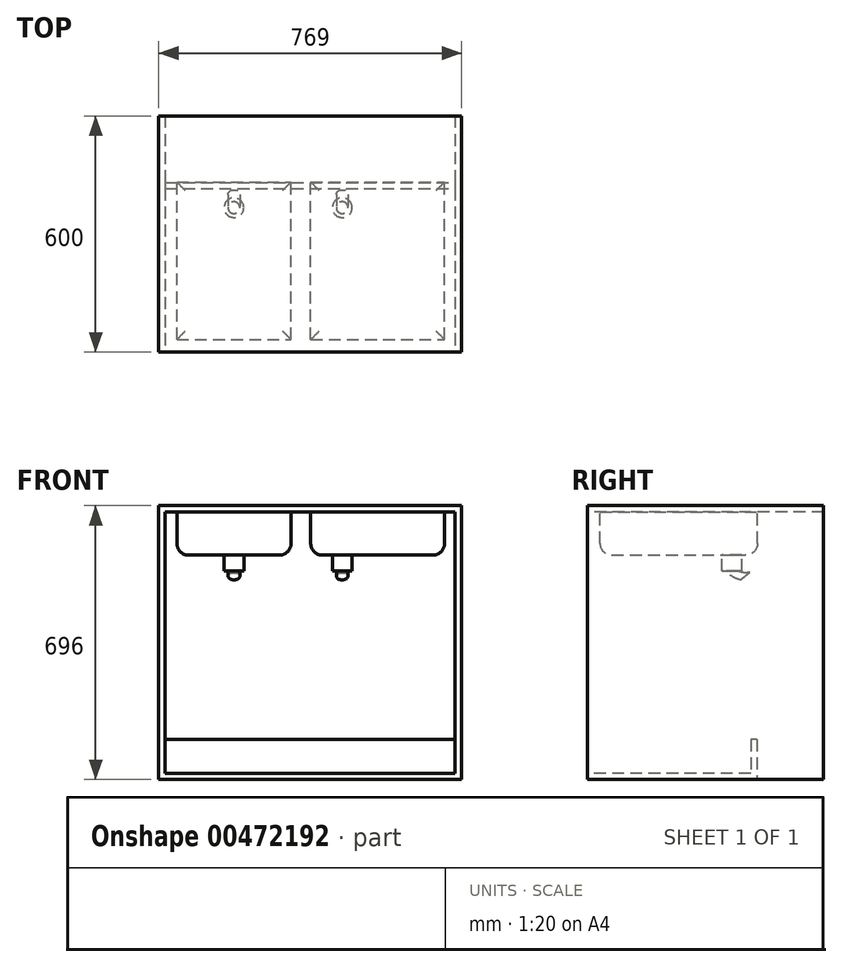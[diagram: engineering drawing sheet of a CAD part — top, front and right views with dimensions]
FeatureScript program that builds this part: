
annotation { "Feature Type Name" : "Feature", "Feature Type Description" : "" }
export const myFeature = defineFeature(function(context is Context, id is Id, definition is map)
    precondition{}
    {
        {
            var Q0;
            Q0=qCreatedBy(makeId("Front.planeOp"),FACE);
            var sketch = newSketch(context, id + "F0", { "sketchPlane" : qUnion([Q0])});
            skLineSegment(sketch, "E0.bottom", {"start": v(0, 0) * mm, "end": v(737, 0) * mm});
            skLineSegment(sketch, "E0.top", {"start": v(0, 664) * mm, "end": v(737, 664) * mm});
            skLineSegment(sketch, "E0.left", {"start": v(0, 0) * mm, "end": v(0, 664) * mm});
            skLineSegment(sketch, "E0.right", {"start": v(737, 0) * mm, "end": v(737, 664) * mm});
            skLineSegment(sketch, "E1.bottom", {"start": v(-16, -16) * mm, "end": v(753, -16) * mm});
            skLineSegment(sketch, "E1.top", {"start": v(-16, 680) * mm, "end": v(753, 680) * mm});
            skLineSegment(sketch, "E1.left", {"start": v(-16, -16) * mm, "end": v(-16, 680) * mm});
            skLineSegment(sketch, "E1.right", {"start": v(753, -16) * mm, "end": v(753, 680) * mm});
            skSolve(sketch);
        }
        {
            var Q0;
            Q0 = qSketchRegion(id + "F0", true);
            extrude(context, id + "F1", {"entities" : qUnion([Q0]), "oppositeDirection" : true, "depth" : 600 * mm});
        }
        {
            var Q0;
            Q0=makeQuery(id+"F1.opExtrude","SWEPT_FACE",FACE,{"disambiguationData":[OSD([sQuery(id+"F0.wireOp",EDGE,"E0.bottom")])]});
            var sketch = newSketch(context, id + "F2", { "sketchPlane" : qUnion([Q0])});
            skLineSegment(sketch, "E2.bottom", {"start": v(0, 415) * mm, "end": v(737, 415) * mm});
            skLineSegment(sketch, "E2.top", {"start": v(0, 431) * mm, "end": v(737, 431) * mm});
            skLineSegment(sketch, "E2.left", {"start": v(0, 415) * mm, "end": v(0, 431) * mm});
            skLineSegment(sketch, "E2.right", {"start": v(737, 415) * mm, "end": v(737, 431) * mm});
            skSolve(sketch);
        }
        {
            var Q0;
            Q0 = qSketchRegion(id + "F2", true);
            extrude(context, id + "F3", {"entities" : qUnion([Q0]), "operationType" : NewBodyOperationType.ADD, "depth" : 86 * mm});
        }
        {
            var Q0;
            Q0=makeQuery(id+"F1.opExtrude","SWEPT_FACE",FACE,{"disambiguationData":[OSD([sQuery(id+"F0.wireOp",EDGE,"E0.top")])]});
            var sketch = newSketch(context, id + "F4", { "sketchPlane" : qUnion([Q0])});
            skLineSegment(sketch, "E3.bottom", {"start": v(30, -32) * mm, "end": v(320, -32) * mm});
            skLineSegment(sketch, "E3.top", {"start": v(30, -432) * mm, "end": v(320, -432) * mm});
            skLineSegment(sketch, "E3.left", {"start": v(30, -32) * mm, "end": v(30, -432) * mm});
            skLineSegment(sketch, "E3.right", {"start": v(320, -32) * mm, "end": v(320, -432) * mm});
            skLineSegment(sketch, "E4.bottom", {"start": v(370, -32) * mm, "end": v(710, -32) * mm});
            skLineSegment(sketch, "E4.top", {"start": v(370, -432) * mm, "end": v(710, -432) * mm});
            skLineSegment(sketch, "E4.left", {"start": v(370, -32) * mm, "end": v(370, -432) * mm});
            skLineSegment(sketch, "E4.right", {"start": v(710, -32) * mm, "end": v(710, -432) * mm});
            skSolve(sketch);
        }
        {
            var Q0;
            Q0 = qSketchRegion(id + "F4", true);
            extrude(context, id + "F5", {"entities" : qUnion([Q0]), "operationType" : NewBodyOperationType.ADD, "depth" : 110 * mm});
        }
        {
            var Q0;
            Q0=makeQuery(id+"F5.opExtrude","CAP_FACE",FACE,{"disambiguationData":[OSD([sQuery(id+"F4.wireOp",EDGE,"E3.bottom"),sQuery(id+"F4.wireOp",EDGE,"E3.top"),sQuery(id+"F4.wireOp",EDGE,"E3.left"),sQuery(id+"F4.wireOp",EDGE,"E3.right")])],"isStart":false});
            var Q1;
            Q1=makeQuery(id+"F5.opExtrude","CAP_FACE",FACE,{"disambiguationData":[OSD([sQuery(id+"F4.wireOp",EDGE,"E4.bottom"),sQuery(id+"F4.wireOp",EDGE,"E4.top"),sQuery(id+"F4.wireOp",EDGE,"E4.left"),sQuery(id+"F4.wireOp",EDGE,"E4.right")])],"isStart":false});
            fillet(context, id + "F6", {"entities" : qUnion([Q0, Q1]), "radius" : 30 * mm, "tangentPropagation" : true, "allowEdgeOverflow" : false});
        }
        {
            var Q0;
            {var subQ2=sQuery(id+"F0.wireOp",EDGE,"E0.bottom");Q0=makeQuery(id+"F3.boolean.opBoolean","SPLIT",FACE,{"disambiguationData":[TD([makeQuery(id+"F3.opExtrude","SWEPT_FACE",FACE,{"disambiguationData":[OSD([sQuery(id+"F2.wireOp",EDGE,"E2.top")])]})])],"derivedFrom":makeQuery(id+"F1.opExtrude","SWEPT_FACE",FACE,{"disambiguationData":[OSD([subQ2])]})});}
            var sketch = newSketch(context, id + "F7", { "sketchPlane" : qUnion([Q0])});
            skLineSegment(sketch, "E5.bottom", {"start": v(0, 431) * mm, "end": v(737, 431) * mm});
            skLineSegment(sketch, "E5.top", {"start": v(0, 600) * mm, "end": v(737, 600) * mm});
            skLineSegment(sketch, "E5.left", {"start": v(0, 431) * mm, "end": v(0, 600) * mm});
            skLineSegment(sketch, "E5.right", {"start": v(737, 431) * mm, "end": v(737, 600) * mm});
            skSolve(sketch);
        }
        {
            var Q0;
            Q0 = qSketchRegion(id + "F7", true);
            extrude(context, id + "F8", {"entities" : qUnion([Q0]), "operationType" : NewBodyOperationType.REMOVE, "endBound" : BoundingType.UP_TO_NEXT, "oppositeDirection" : true, "depth" : 25 * mm});
        }
        {
            var Q0;
            Q0=makeQuery(id+"F5.opExtrude","CAP_FACE",FACE,{"disambiguationData":[OSD([sQuery(id+"F4.wireOp",EDGE,"E3.bottom"),sQuery(id+"F4.wireOp",EDGE,"E3.top"),sQuery(id+"F4.wireOp",EDGE,"E3.left"),sQuery(id+"F4.wireOp",EDGE,"E3.right")])],"isStart":false});
            var sketch = newSketch(context, id + "F9", { "sketchPlane" : qUnion([Q0])});
            skCircle(sketch, "E6", {"center": v(175, -367) * mm, "radius": 25 * mm});
            skSolve(sketch);
        }
        {
            var Q0;
            Q0 = qSketchRegion(id + "F9", true);
            extrude(context, id + "F10", {"entities" : qUnion([Q0]), "operationType" : NewBodyOperationType.ADD, "depth" : 40 * mm});
        }
        {
            var Q0;
            Q0=makeQuery(id+"F5.opExtrude","CAP_FACE",FACE,{"disambiguationData":[OSD([sQuery(id+"F4.wireOp",EDGE,"E4.bottom"),sQuery(id+"F4.wireOp",EDGE,"E4.top"),sQuery(id+"F4.wireOp",EDGE,"E4.left"),sQuery(id+"F4.wireOp",EDGE,"E4.right")])],"isStart":false});
            var sketch = newSketch(context, id + "F11", { "sketchPlane" : qUnion([Q0])});
            skCircle(sketch, "E7", {"center": v(450, -367) * mm, "radius": 25 * mm});
            skSolve(sketch);
        }
        {
            var Q0;
            Q0 = qSketchRegion(id + "F11", true);
            extrude(context, id + "F12", {"entities" : qUnion([Q0]), "operationType" : NewBodyOperationType.ADD, "depth" : 40 * mm});
        }
        {
            var Q0;
            Q0=makeQuery(id+"F12.opExtrude","CAP_FACE",FACE,{"disambiguationData":[OSD([sQuery(id+"F11.wireOp",EDGE,"E7")])],"isStart":false});
            var sketch = newSketch(context, id + "F13", { "sketchPlane" : qUnion([Q0])});
            skCircle(sketch, "E8", {"center": v(450, -367) * mm, "radius": 15 * mm});
            skSolve(sketch);
        }
        {
            var Q0;
            Q0 = qSketchRegion(id + "F13", true);
            var Q1;
            {var subQ0=sQuery(id+"F4.wireOp",EDGE,"E4.top");Q1=makeQuery(id+"F6.opFillet","BLEND_EDGE",EDGE,{"blendedFrom":[makeQuery(id+"F5.opExtrude","CAP_EDGE",EDGE,{"disambiguationData":[OSD([subQ0])],"isStart":false}),makeQuery(id+"F5.opExtrude","CAP_FACE",FACE,{"disambiguationData":[OSD([sQuery(id+"F4.wireOp",EDGE,"E4.bottom"),subQ0,sQuery(id+"F4.wireOp",EDGE,"E4.left"),sQuery(id+"F4.wireOp",EDGE,"E4.right")])],"isStart":false})],"blendedInto":[makeQuery(id+"F5.opExtrude","CAP_FACE",FACE,{"disambiguationData":[OSD([sQuery(id+"F4.wireOp",EDGE,"E4.bottom"),subQ0,sQuery(id+"F4.wireOp",EDGE,"E4.left"),sQuery(id+"F4.wireOp",EDGE,"E4.right")])],"isStart":false})]});}
            revolve(context, id + "F14", {"operationType" : NewBodyOperationType.ADD, "entities" : qUnion([Q0]), "axis" : qUnion([Q1]), "revolveType" : RevolveType.ONE_DIRECTION, "angle" : 40 * degree});
        }
        {
            var Q0;
            Q0=makeQuery(id+"F10.opExtrude","CAP_FACE",FACE,{"disambiguationData":[OSD([sQuery(id+"F9.wireOp",EDGE,"E6")])],"isStart":false});
            var sketch = newSketch(context, id + "F15", { "sketchPlane" : qUnion([Q0])});
            skCircle(sketch, "E9", {"center": v(175, -367) * mm, "radius": 15 * mm});
            skSolve(sketch);
        }
        {
            var Q0;
            Q0 = qSketchRegion(id + "F15", true);
            var Q1;
            {var subQ0=sQuery(id+"F4.wireOp",EDGE,"E3.top");Q1=makeQuery(id+"F6.opFillet","BLEND_EDGE",EDGE,{"blendedFrom":[makeQuery(id+"F5.opExtrude","CAP_EDGE",EDGE,{"disambiguationData":[OSD([subQ0])],"isStart":false}),makeQuery(id+"F5.opExtrude","CAP_FACE",FACE,{"disambiguationData":[OSD([sQuery(id+"F4.wireOp",EDGE,"E3.bottom"),subQ0,sQuery(id+"F4.wireOp",EDGE,"E3.left"),sQuery(id+"F4.wireOp",EDGE,"E3.right")])],"isStart":false})],"blendedInto":[makeQuery(id+"F5.opExtrude","CAP_FACE",FACE,{"disambiguationData":[OSD([sQuery(id+"F4.wireOp",EDGE,"E3.bottom"),subQ0,sQuery(id+"F4.wireOp",EDGE,"E3.left"),sQuery(id+"F4.wireOp",EDGE,"E3.right")])],"isStart":false})]});}
            revolve(context, id + "F16", {"operationType" : NewBodyOperationType.ADD, "entities" : qUnion([Q0]), "axis" : qUnion([Q1]), "revolveType" : RevolveType.ONE_DIRECTION, "angle" : 40 * degree});
        }
    });
